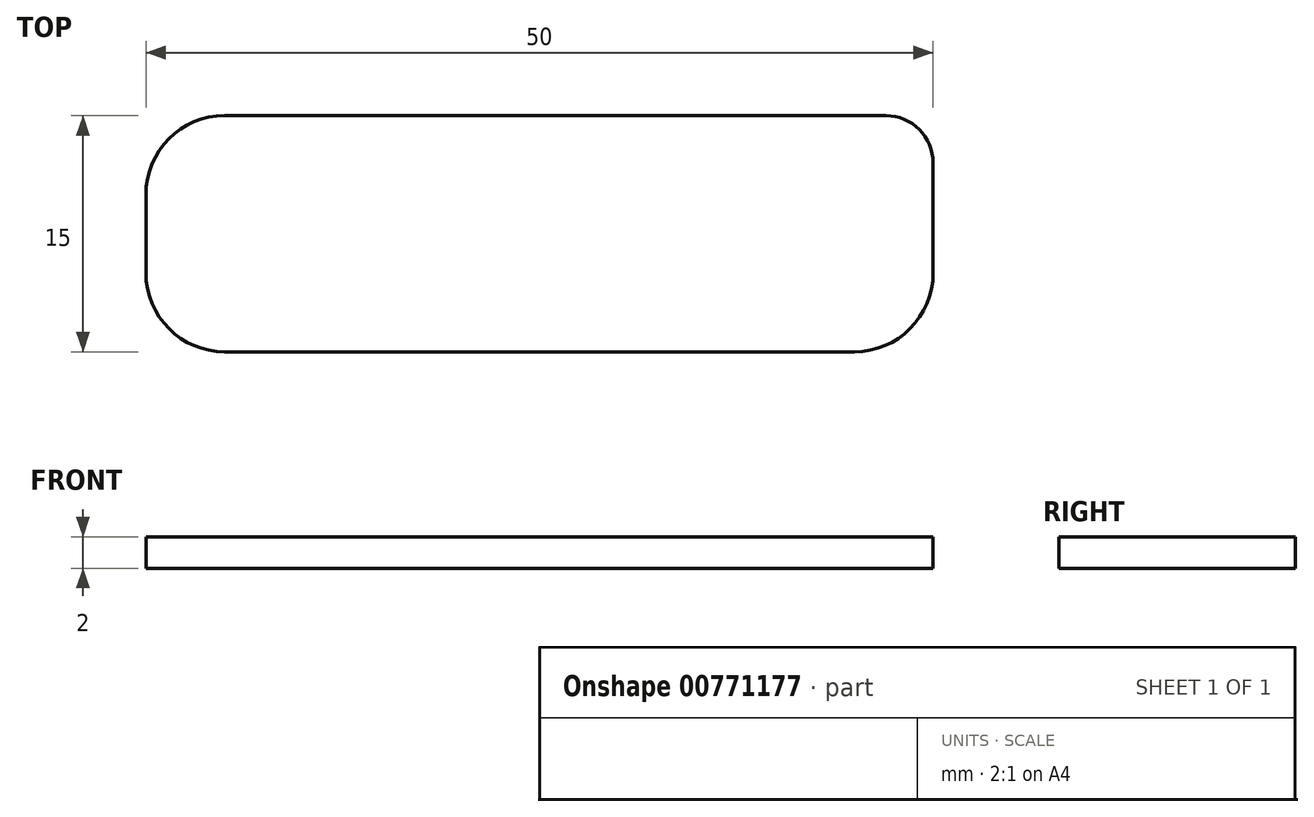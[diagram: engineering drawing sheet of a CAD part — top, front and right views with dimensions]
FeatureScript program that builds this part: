
annotation { "Feature Type Name" : "Feature", "Feature Type Description" : "" }
export const myFeature = defineFeature(function(context is Context, id is Id, definition is map)
    precondition{}
    {
        {
            var Q0;
            Q0=qCreatedBy(makeId("Top.planeOp"),FACE);
            var sketch = newSketch(context, id + "F0", { "sketchPlane" : qUnion([Q0])});
            skLineSegment(sketch, "E0.bottom", {"start": v(0, 0) * mm, "end": v(-50, 0) * mm});
            skLineSegment(sketch, "E0.top", {"start": v(0, 15) * mm, "end": v(-50, 15) * mm});
            skLineSegment(sketch, "E0.left", {"start": v(0, 0) * mm, "end": v(0, 15) * mm});
            skLineSegment(sketch, "E0.right", {"start": v(-50, 0) * mm, "end": v(-50, 15) * mm});
            skSolve(sketch);
        }
        {
            var Q0;
            Q0 = qSketchRegion(id + "F0", true);
            extrude(context, id + "F1", {"entities" : qUnion([Q0]), "depth" : 2 * mm, "offsetDistance" : 25 * mm});
        }
        {
            var Q0;
            Q0=makeQuery(id+"F1.opExtrude","SWEPT_EDGE",EDGE,{"disambiguationData":[OSD([sQuery(id+"F0.wireOp",EDGE,"E0.top"),sQuery(id+"F0.wireOp",EDGE,"E0.left")])]});
            fillet(context, id + "F2", {"entities" : qUnion([Q0]), "radius" : 3 * mm, "tangentPropagation" : true, "allowEdgeOverflow" : false});
        }
        {
            var Q0;
            Q0=makeQuery(id+"F1.opExtrude","SWEPT_EDGE",EDGE,{"disambiguationData":[OSD([sQuery(id+"F0.wireOp",EDGE,"E0.bottom"),sQuery(id+"F0.wireOp",EDGE,"E0.left")])]});
            fillet(context, id + "F3", {"entities" : qUnion([Q0]), "radius" : 5 * mm, "tangentPropagation" : true, "allowEdgeOverflow" : false});
        }
        {
            var Q0;
            Q0=makeQuery(id+"F1.opExtrude","SWEPT_EDGE",EDGE,{"disambiguationData":[OSD([sQuery(id+"F0.wireOp",EDGE,"E0.top"),sQuery(id+"F0.wireOp",EDGE,"E0.right")])]});
            var Q1;
            Q1=makeQuery(id+"F1.opExtrude","SWEPT_EDGE",EDGE,{"disambiguationData":[OSD([sQuery(id+"F0.wireOp",EDGE,"E0.bottom"),sQuery(id+"F0.wireOp",EDGE,"E0.right")])]});
            fillet(context, id + "F4", {"entities" : qUnion([Q0, Q1]), "radius" : 5 * mm, "tangentPropagation" : true, "allowEdgeOverflow" : false});
        }
    });
